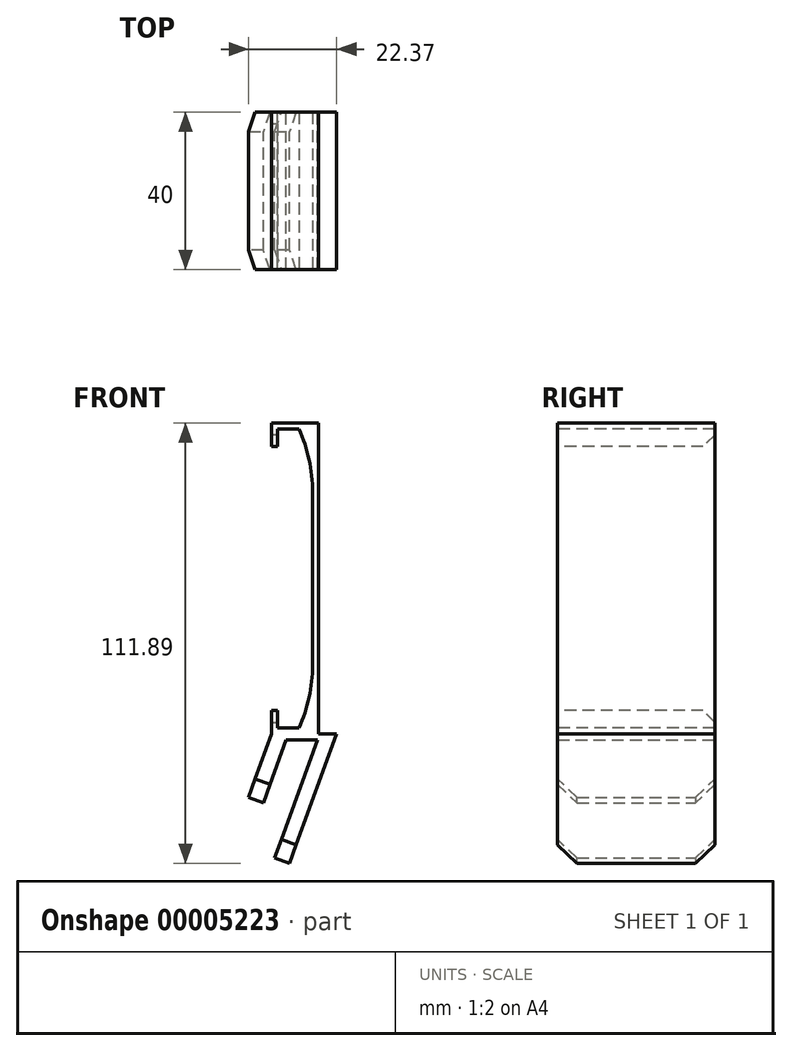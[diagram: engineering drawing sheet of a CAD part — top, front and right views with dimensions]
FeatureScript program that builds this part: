
annotation { "Feature Type Name" : "Feature", "Feature Type Description" : "" }
export const myFeature = defineFeature(function(context is Context, id is Id, definition is map)
    precondition{}
    {
        {
            var Q0;
            Q0=qCreatedBy(makeId("Front.planeOp"),FACE);
            var sketch = newSketch(context, id + "F0", { "sketchPlane" : qUnion([Q0])});
            skLineSegment(sketch, "E0.rect.bottom", {"start": v(4.45, 38) * mm, "end": v(-4.45, 38) * mm});
            skLineSegment(sketch, "E0.rect.top", {"start": v(4.45, -38) * mm, "end": v(-4.45, -38) * mm});
            skLineSegment(sketch, "E0.rect.left", {"start": v(4.45, 38) * mm, "end": v(4.45, -38) * mm});
            skLineSegment(sketch, "E0.rect.right", {"start": v(-4.45, 38) * mm, "end": v(-4.45, -38) * mm});
            skPoint(sketch, "E0.rect.middle", {"position": v(0, 0) * mm});
            skLineSegment(sketch, "E1.0", {"start": v(-5.95, 39.5) * mm, "end": v(-5.95, -39.5) * mm});
            skLineSegment(sketch, "E1.1", {"start": v(5.95, 39.5) * mm, "end": v(-5.95, 39.5) * mm});
            skLineSegment(sketch, "E1.2", {"start": v(5.95, 39.5) * mm, "end": v(5.95, -39.5) * mm});
            skLineSegment(sketch, "E1.3", {"start": v(5.95, -39.5) * mm, "end": v(-5.95, -39.5) * mm});
            skSolve(sketch);
        }
        {
            var Q0;
            Q0=qSketchRegion(id+"F0",true);
            extrude(context, id + "F1", {"entities" : qUnion([Q0]), "depth" : 40 * mm, "symmetric" : true});
        }
        {
            var Q0;
            Q0=makeQuery(id+"F1.opExtrude","CAP_FACE",FACE,{"disambiguationData":[OSD([sQuery(id+"F0.wireOp",EDGE,"E0.rect.bottom"),sQuery(id+"F0.wireOp",EDGE,"E0.rect.top"),sQuery(id+"F0.wireOp",EDGE,"E0.rect.left"),sQuery(id+"F0.wireOp",EDGE,"E0.rect.right"),sQuery(id+"F0.wireOp",EDGE,"E1.0"),sQuery(id+"F0.wireOp",EDGE,"E1.1"),sQuery(id+"F0.wireOp",EDGE,"E1.2"),sQuery(id+"F0.wireOp",EDGE,"E1.3")])],"isStart":false});
            var sketch = newSketch(context, id + "F2", { "sketchPlane" : qUnion([Q0])});
            skLineSegment(sketch, "E2", {"start": v(4.45, 0) * mm, "end": v(-4.45, 0) * mm, "construction": true});
            skLineSegment(sketch, "E3.bottom", {"start": v(-5.95, 33.5) * mm, "end": v(-4.45, 33.5) * mm});
            skLineSegment(sketch, "E3.top", {"start": v(-5.95, -33.5) * mm, "end": v(-4.45, -33.5) * mm});
            skLineSegment(sketch, "E3.left", {"start": v(-5.95, 33.5) * mm, "end": v(-5.95, -33.5) * mm});
            skLineSegment(sketch, "E3.right", {"start": v(-4.45, 33.5) * mm, "end": v(-4.45, -33.5) * mm});
            skPoint(sketch, "E4", {"position": v(-4.45, 0) * mm});
            skSolve(sketch);
        }
        {
            var Q0;
            Q0=qSketchRegion(id+"F2",true);
            extrude(context, id + "F3", {"entities" : qUnion([Q0]), "operationType" : NewBodyOperationType.REMOVE, "endBound" : BoundingType.THROUGH_ALL, "oppositeDirection" : true, "depth" : 25 * mm});
        }
        {
            var Q0;
            Q0=makeQuery(id+"F1.opExtrude","CAP_FACE",FACE,{"disambiguationData":[OSD([sQuery(id+"F0.wireOp",EDGE,"E0.rect.bottom"),sQuery(id+"F0.wireOp",EDGE,"E0.rect.top"),sQuery(id+"F0.wireOp",EDGE,"E0.rect.left"),sQuery(id+"F0.wireOp",EDGE,"E0.rect.right"),sQuery(id+"F0.wireOp",EDGE,"E1.0"),sQuery(id+"F0.wireOp",EDGE,"E1.1"),sQuery(id+"F0.wireOp",EDGE,"E1.2"),sQuery(id+"F0.wireOp",EDGE,"E1.3")])],"isStart":false});
            var sketch = newSketch(context, id + "F4", { "sketchPlane" : qUnion([Q0])});
            skLineSegment(sketch, "E5", {"start": v(4.45, 0) * mm, "end": v(-27.44, 0) * mm, "construction": true});
            skArc(sketch, "E6", {"start": v(4.45, 22) * mm, "mid": v(3.6, 30.18) * mm, "end": v(1.05, 38) * mm});
            skLineSegment(sketch, "E7", {"start": v(1.05, 38) * mm, "end": v(4.45, 38) * mm});
            skLineSegment(sketch, "E8", {"start": v(4.45, 38) * mm, "end": v(4.45, 22) * mm});
            skLineSegment(sketch, "E9.0.MirrorCS", {"start": v(1.05, -38) * mm, "end": v(4.45, -38) * mm});
            skLineSegment(sketch, "E9.1.MirrorCS", {"start": v(4.45, -38) * mm, "end": v(4.45, -22) * mm});
            skArc(sketch, "E9.2.MirrorCS", {"start": v(4.45, -22) * mm, "mid": v(3.6, -30.18) * mm, "end": v(1.05, -38) * mm});
            skSolve(sketch);
        }
        {
            var Q0;
            Q0=qSketchRegion(id+"F4",true);
            var Q1;
            Q1=makeQuery(id+"F1.opExtrude","CAP_FACE",FACE,{"disambiguationData":[OSD([sQuery(id+"F0.wireOp",EDGE,"E0.rect.bottom"),sQuery(id+"F0.wireOp",EDGE,"E0.rect.top"),sQuery(id+"F0.wireOp",EDGE,"E0.rect.left"),sQuery(id+"F0.wireOp",EDGE,"E0.rect.right"),sQuery(id+"F0.wireOp",EDGE,"E1.0"),sQuery(id+"F0.wireOp",EDGE,"E1.1"),sQuery(id+"F0.wireOp",EDGE,"E1.2"),sQuery(id+"F0.wireOp",EDGE,"E1.3")])],"isStart":true});
            extrude(context, id + "F5", {"entities" : qUnion([Q0]), "operationType" : NewBodyOperationType.ADD, "endBound" : BoundingType.UP_TO_SURFACE, "oppositeDirection" : true, "endBoundEntityFace" : qUnion([Q1]), "depth" : 25 * mm});
        }
        {
            var Q0;
            Q0=makeQuery(id+"F3.boolean.opBoolean","COPY",EDGE,{"derivedFrom":makeQuery(id+"F3.opExtrude","CAP_EDGE",EDGE,{"disambiguationData":[OSD([sQuery(id+"F2.wireOp",EDGE,"E3.bottom")])],"isStart":true})});
            var Q1;
            Q1=makeQuery(id+"F3.boolean.opBoolean","INTERSECT",EDGE,{"derivedFrom":[makeQuery(id+"F1.opExtrude","CAP_FACE",FACE,{"disambiguationData":[OSD([sQuery(id+"F0.wireOp",EDGE,"E0.rect.bottom"),sQuery(id+"F0.wireOp",EDGE,"E0.rect.top"),sQuery(id+"F0.wireOp",EDGE,"E0.rect.left"),sQuery(id+"F0.wireOp",EDGE,"E0.rect.right"),sQuery(id+"F0.wireOp",EDGE,"E1.0"),sQuery(id+"F0.wireOp",EDGE,"E1.1"),sQuery(id+"F0.wireOp",EDGE,"E1.2"),sQuery(id+"F0.wireOp",EDGE,"E1.3")])],"isStart":true}),makeQuery(id+"F3.opExtrude","SWEPT_FACE",FACE,{"disambiguationData":[OSD([sQuery(id+"F2.wireOp",EDGE,"E3.bottom")])]})]});
            var Q2;
            Q2=makeQuery(id+"F3.boolean.opBoolean","INTERSECT",EDGE,{"derivedFrom":[makeQuery(id+"F1.opExtrude","CAP_FACE",FACE,{"disambiguationData":[OSD([sQuery(id+"F0.wireOp",EDGE,"E0.rect.bottom"),sQuery(id+"F0.wireOp",EDGE,"E0.rect.top"),sQuery(id+"F0.wireOp",EDGE,"E0.rect.left"),sQuery(id+"F0.wireOp",EDGE,"E0.rect.right"),sQuery(id+"F0.wireOp",EDGE,"E1.0"),sQuery(id+"F0.wireOp",EDGE,"E1.1"),sQuery(id+"F0.wireOp",EDGE,"E1.2"),sQuery(id+"F0.wireOp",EDGE,"E1.3")])],"isStart":true}),makeQuery(id+"F3.opExtrude","SWEPT_FACE",FACE,{"disambiguationData":[OSD([sQuery(id+"F2.wireOp",EDGE,"E3.top")])]})]});
            var Q3;
            Q3=makeQuery(id+"F3.boolean.opBoolean","COPY",EDGE,{"derivedFrom":makeQuery(id+"F3.opExtrude","CAP_EDGE",EDGE,{"disambiguationData":[OSD([sQuery(id+"F2.wireOp",EDGE,"E3.top")])],"isStart":true})});
            chamfer(context, id + "F6", {"entities" : qUnion([Q0, Q1, Q2, Q3]), "width" : 3 * mm, "tangentPropagation" : true});
        }
        {
            var Q0;
            Q0=qCreatedBy(makeId("Front.planeOp"),FACE);
            var sketch = newSketch(context, id + "F7", { "sketchPlane" : qUnion([Q0])});
            skLineSegment(sketch, "E10.0", {"start": v(5.95, -39.5) * mm, "end": v(-5.95, -39.5) * mm});
            skLineSegment(sketch, "E11", {"start": v(-5.95, -39.5) * mm, "end": v(-11.81, -55.6) * mm});
            skLineSegment(sketch, "E12", {"start": v(-11.81, -55.6) * mm, "end": v(-8.05, -56.97) * mm});
            skLineSegment(sketch, "E13", {"start": v(-8.05, -56.97) * mm, "end": v(-2.24, -41) * mm});
            skLineSegment(sketch, "E14", {"start": v(-2.24, -41) * mm, "end": v(5.76, -41) * mm});
            skLineSegment(sketch, "E15", {"start": v(5.76, -41) * mm, "end": v(-5.17, -71.02) * mm});
            skLineSegment(sketch, "E16", {"start": v(-5.17, -71.02) * mm, "end": v(-1.4, -72.39) * mm});
            skLineSegment(sketch, "E17", {"start": v(-1.4, -72.39) * mm, "end": v(10.56, -39.5) * mm});
            skLineSegment(sketch, "E18", {"start": v(5.95, -39.5) * mm, "end": v(10.56, -39.5) * mm});
            skSolve(sketch);
        }
        {
            var Q0;
            Q0 = qSketchRegion(id + "F7", true);
            extrude(context, id + "F8", {"entities" : qUnion([Q0]), "operationType" : NewBodyOperationType.ADD, "depth" : 40 * mm, "symmetric" : true});
        }
        {
            var Q0;
            Q0=makeQuery(id+"F1.opExtrude","SWEPT_EDGE",EDGE,{"disambiguationData":[OSD([sQuery(id+"F0.wireOp",EDGE,"E1.2"),sQuery(id+"F0.wireOp",EDGE,"E1.3")])]});
            var Q1;
            Q1=makeQuery(id+"F8.opExtrude","CAP_EDGE",EDGE,{"disambiguationData":[OSD([sQuery(id+"F7.wireOp",EDGE,"E12")])],"isStart":false});
            var Q2;
            Q2=makeQuery(id+"F8.opExtrude","CAP_EDGE",EDGE,{"disambiguationData":[OSD([sQuery(id+"F7.wireOp",EDGE,"E16")])],"isStart":false});
            var Q3;
            Q3=makeQuery(id+"F8.opExtrude","CAP_EDGE",EDGE,{"disambiguationData":[OSD([sQuery(id+"F7.wireOp",EDGE,"E16")])],"isStart":true});
            var Q4;
            Q4=makeQuery(id+"F8.opExtrude","CAP_EDGE",EDGE,{"disambiguationData":[OSD([sQuery(id+"F7.wireOp",EDGE,"E12")])],"isStart":true});
            chamfer(context, id + "F9", {"entities" : qUnion([Q0, Q1, Q2, Q3, Q4]), "width" : 5 * mm, "tangentPropagation" : true});
        }
    });
